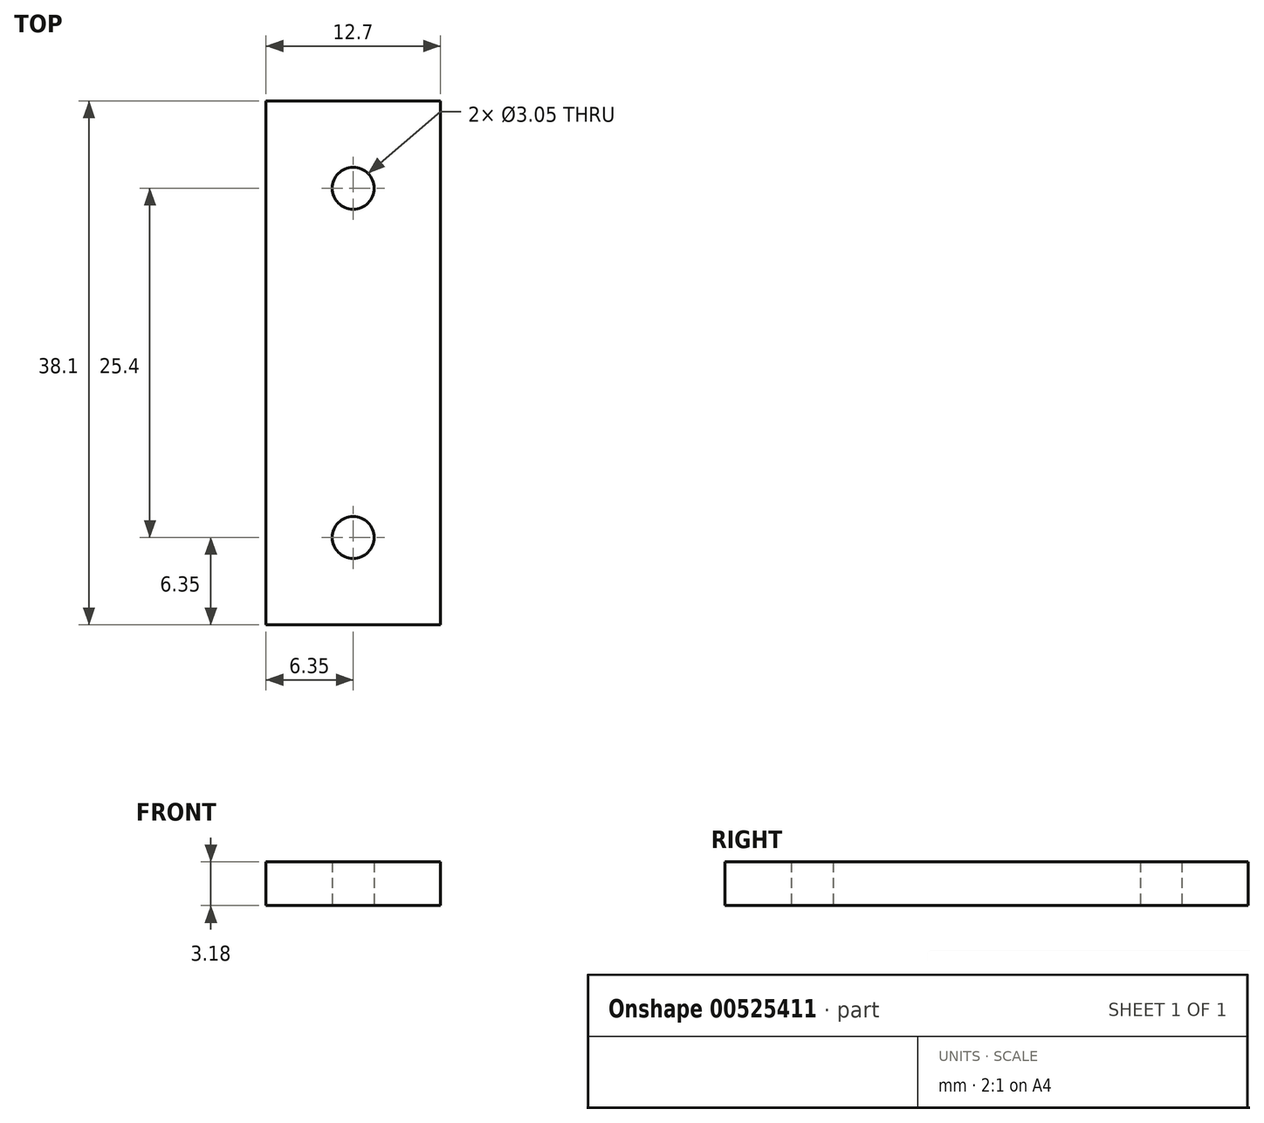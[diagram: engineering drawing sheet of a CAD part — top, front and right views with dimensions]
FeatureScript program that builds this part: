
annotation { "Feature Type Name" : "Feature", "Feature Type Description" : "" }
export const myFeature = defineFeature(function(context is Context, id is Id, definition is map)
    precondition{}
    {
        {
            var Q0;
            Q0=qCreatedBy(makeId("Top.planeOp"),FACE);
            var sketch = newSketch(context, id + "F0", { "sketchPlane" : qUnion([Q0])});
            skLineSegment(sketch, "E0.bottom", {"start": v(-6.35, 19.05) * mm, "end": v(6.35, 19.05) * mm});
            skLineSegment(sketch, "E0.top", {"start": v(-6.35, -19.05) * mm, "end": v(6.35, -19.05) * mm});
            skLineSegment(sketch, "E0.left", {"start": v(-6.35, 19.05) * mm, "end": v(-6.35, -19.05) * mm});
            skLineSegment(sketch, "E0.right", {"start": v(6.35, 19.05) * mm, "end": v(6.35, -19.05) * mm});
            skPoint(sketch, "E0.middle", {"position": v(0, 0) * mm});
            skCircle(sketch, "E1", {"center": v(0, -12.7) * mm, "radius": 1.52 * mm});
            skCircle(sketch, "E2.MirrorC", {"center": v(0, 12.7) * mm, "radius": 1.52 * mm});
            skSolve(sketch);
        }
        {
            var Q0;
            Q0=makeQuery(id+"F0.imprint","IMPRINT",FACE,{"disambiguationData":[TD([[makeQuery(id+"F0.imprint","IMPRINT",EDGE,{"derivedFrom":sQuery(id+"F0.wireOp",EDGE,"E0.bottom")}),-1.0]])]});
            extrude(context, id + "F1", {"entities" : qUnion([Q0]), "depth" : 3.17 * mm, "offsetDistance" : 25.4 * mm});
        }
    });
